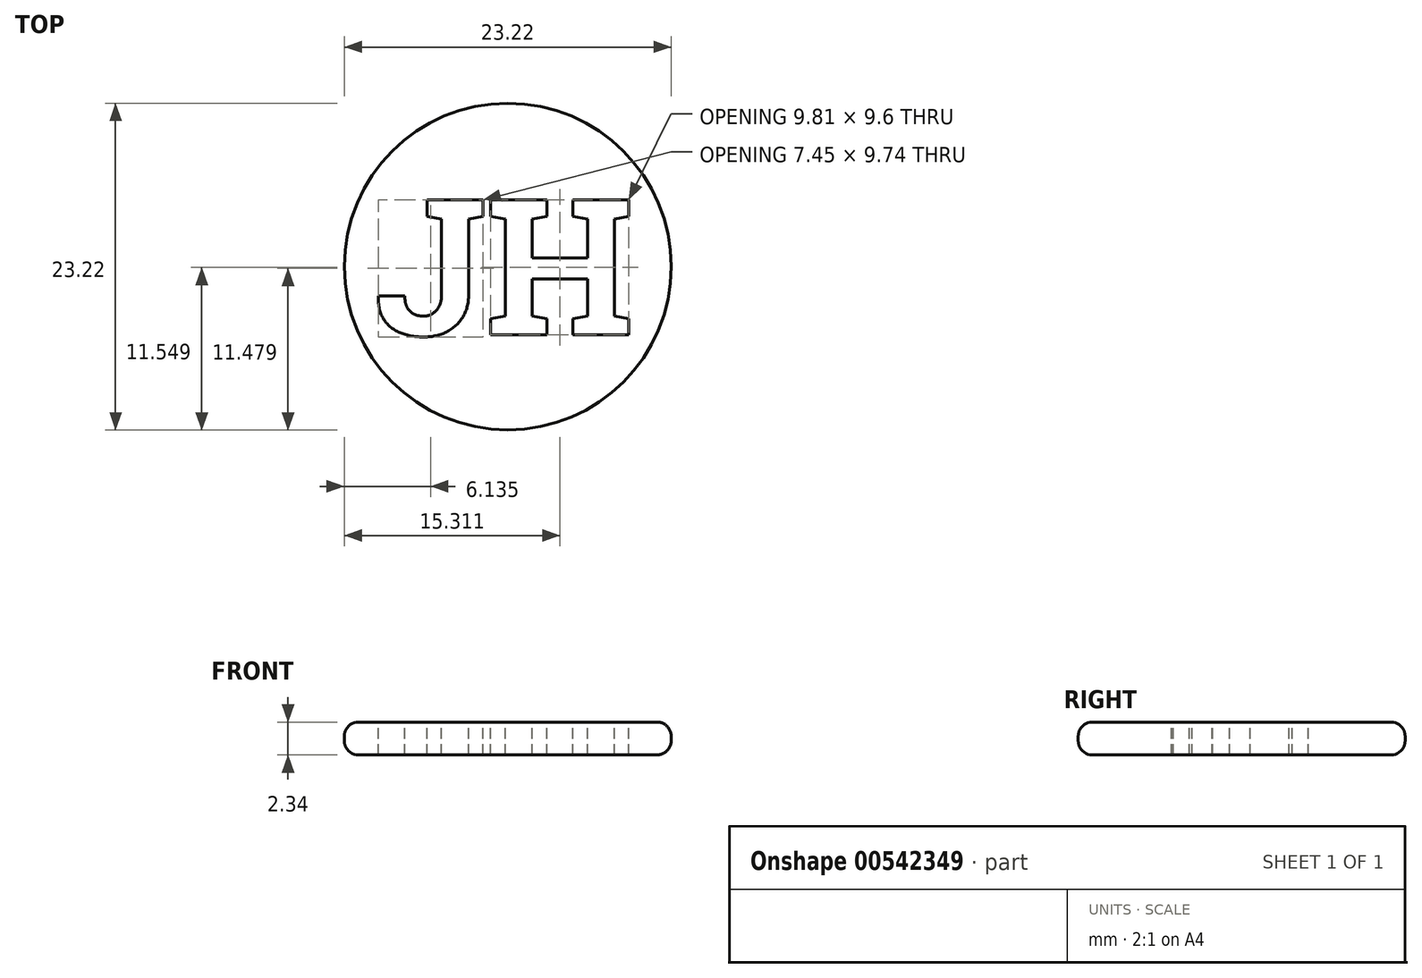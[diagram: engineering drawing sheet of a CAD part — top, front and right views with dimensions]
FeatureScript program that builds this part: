
annotation { "Feature Type Name" : "Feature", "Feature Type Description" : "" }
export const myFeature = defineFeature(function(context is Context, id is Id, definition is map)
    precondition{}
    {
        {
            var Q0;
            Q0=qCreatedBy(makeId("Top.planeOp"),FACE);
            var sketch = newSketch(context, id + "F0", { "sketchPlane" : qUnion([Q0])});
            skCircle(sketch, "E0", {"center": v(0, 0) * mm, "radius": 11.6 * mm});
            skSolve(sketch);
        }
        {
            var Q0;
            Q0 = qSketchRegion(id + "F0", true);
            extrude(context, id + "F1", {"entities" : qUnion([Q0]), "endBound" : BoundingType.SYMMETRIC, "depth" : 2.33 * mm, "offsetDistance" : 25 * mm});
        }
        {
            var Q0;
            Q0=makeQuery(id+"F1.opExtrude","CAP_EDGE",EDGE,{"disambiguationData":[OSD([sQuery(id+"F0.wireOp",EDGE,"E0")])],"isStart":false});
            var Q1;
            Q1=makeQuery(id+"F1.opExtrude","CAP_EDGE",EDGE,{"disambiguationData":[OSD([sQuery(id+"F0.wireOp",EDGE,"E0")])],"isStart":true});
            fillet(context, id + "F2", {"entities" : qUnion([Q0, Q1]), "radius" : 1 * mm, "tangentPropagation" : true, "allowEdgeOverflow" : false});
        }
        {
            var Q0;
            Q0=makeQuery(id+"F1.opExtrude","CAP_FACE",FACE,{"disambiguationData":[OSD([sQuery(id+"F0.wireOp",EDGE,"E0")])],"isStart":false});
            var sketch = newSketch(context, id + "F3", { "sketchPlane" : qUnion([Q0])});
            skText(sketch, "E1", { "text": "JH", "fontName": "RobotoSlab-Bold.ttf"});
            const initialGuessF3  = {"E1": [-0.00943, -0.00486, 1, 0, 0.00972]};
            skSetInitialGuess(sketch, initialGuessF3);
            skSolve(sketch);
        }
        {
            var Q0;
            Q0 = qSketchRegion(id + "F3", true);
            extrude(context, id + "F4", {"entities" : qUnion([Q0]), "operationType" : NewBodyOperationType.REMOVE, "endBound" : BoundingType.THROUGH_ALL, "oppositeDirection" : true, "depth" : 25 * mm, "offsetDistance" : 25 * mm});
        }
    });
